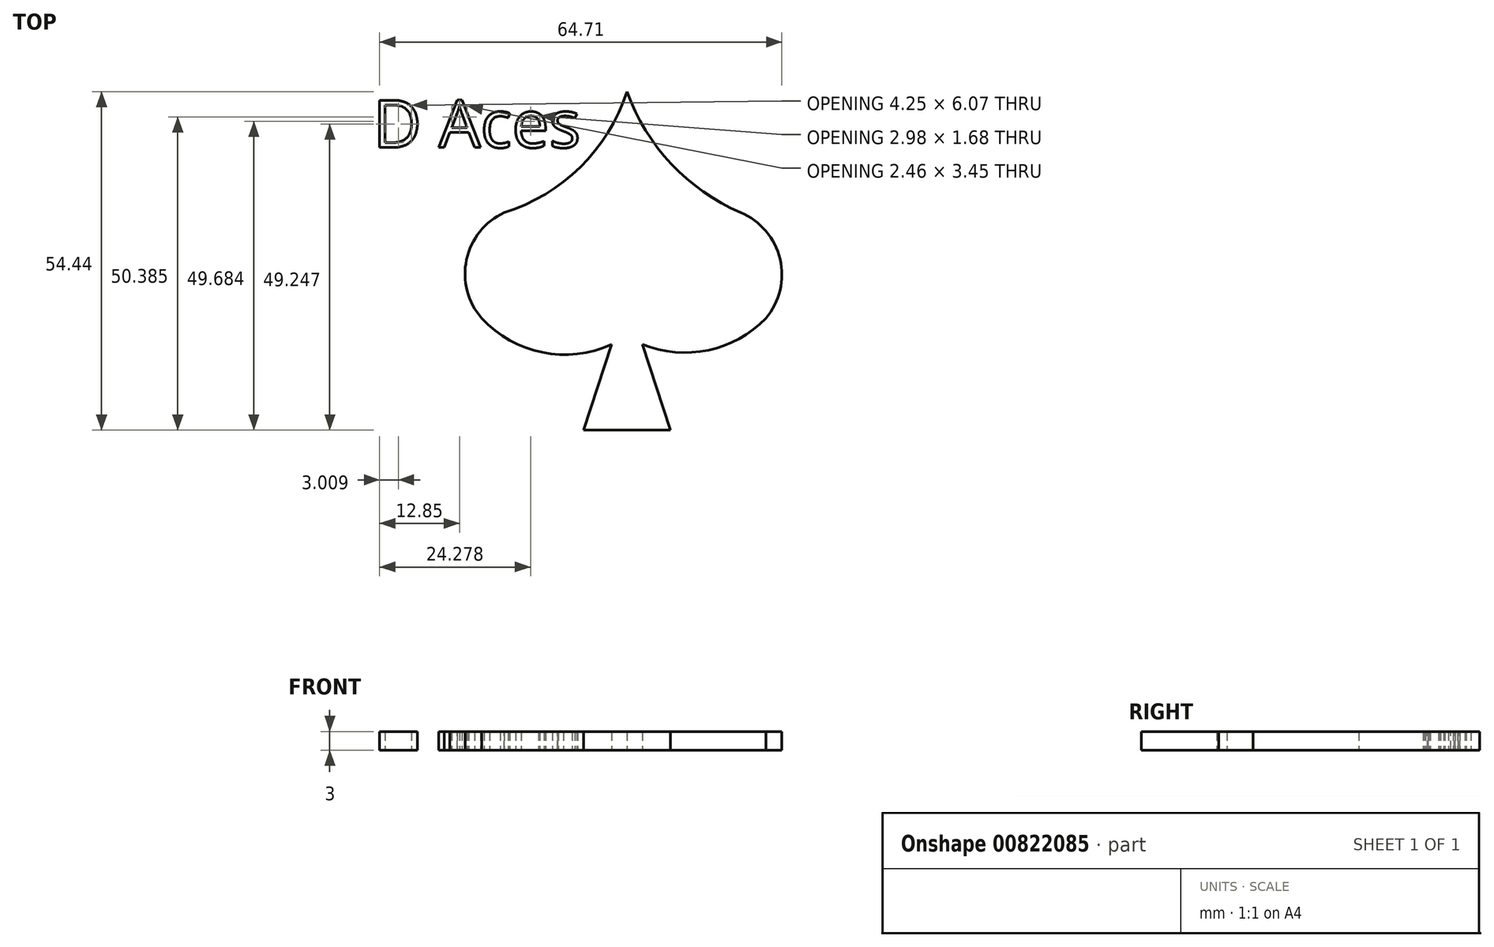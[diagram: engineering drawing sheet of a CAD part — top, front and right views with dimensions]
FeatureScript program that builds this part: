
annotation { "Feature Type Name" : "Feature", "Feature Type Description" : "" }
export const myFeature = defineFeature(function(context is Context, id is Id, definition is map)
    precondition{}
    {
        {
            var Q0;
            Q0=qCreatedBy(makeId("Top.planeOp"),FACE);
            var sketch = newSketch(context, id + "F0", { "sketchPlane" : qUnion([Q0])});
            skLineSegment(sketch, "E0", {"start": v(-7, -29.2) * mm, "end": v(7, -29.2) * mm});
            skLineSegment(sketch, "E1", {"start": v(-7, -29.2) * mm, "end": v(-2.5, -15.42) * mm});
            skLineSegment(sketch, "E2", {"start": v(7, -29.2) * mm, "end": v(2.49, -15.42) * mm});
            skArc(sketch, "E3", {"start": v(-23.36, -11.2) * mm, "mid": v(-13.6, -16.7) * mm, "end": v(-2.5, -15.42) * mm});
            skArc(sketch, "E4", {"start": v(2.49, -15.42) * mm, "mid": v(13.07, -16.36) * mm, "end": v(22.36, -11.2) * mm});
            skArc(sketch, "E5", {"start": v(-19.75, 5.79) * mm, "mid": v(-25.8, -1.8) * mm, "end": v(-23.36, -11.2) * mm});
            skArc(sketch, "E6", {"start": v(22.36, -11.2) * mm, "mid": v(24.63, -1.68) * mm, "end": v(18.3, 5.79) * mm});
            skArc(sketch, "E7", {"start": v(-19.75, 5.79) * mm, "mid": v(-7.5, 13.1) * mm, "end": v(0, 25.24) * mm});
            skArc(sketch, "E8", {"start": v(0, 25.24) * mm, "mid": v(7.13, 13.6) * mm, "end": v(18.3, 5.79) * mm});
            skText(sketch, "E9", { "text": "D Aces\n", "fontName": "OpenSans-Regular.ttf"});
            const initialGuessF0  = {"E9": [-0.04083, 0.01625, 1, 0, 0.00766]};
            skSetInitialGuess(sketch, initialGuessF0);
            skSolve(sketch);
        }
        {
            var Q0;
            Q0 = qSketchRegion(id + "F0", true);
            extrude(context, id + "F1", {"entities" : qUnion([Q0]), "depth" : 3 * mm, "offsetDistance" : 25 * mm});
        }
    });
